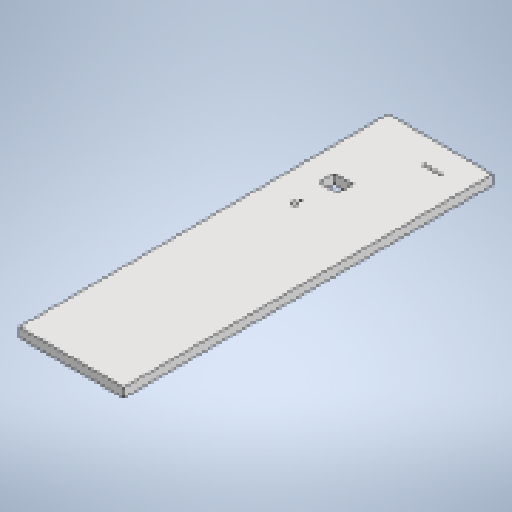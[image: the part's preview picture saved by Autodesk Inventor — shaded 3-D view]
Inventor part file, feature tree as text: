
AUTODESK INVENTOR PART (.ipt)
format: ipt  version: 2025 (Build 290162010, 162A)  size: 158,720 bytes
history: native  units: mm
features: extrude x1, sketch x1
ambient origin geometry x8: Origin, YZ Plane, XZ Plane, XY Plane, X Axis, Y Axis, Z Axis, Center Point
bodies: Solid1 (feature_tree)
feature tree (2):
  extrude  "Extrusion1"  Depth=12000.0mm
  sketch  "Sketch1"  dims[d0=3400.0mm d1=12000.0mm d2=600.0mm d3=500.0mm d4=168.0mm d5=63.0mm d6=1000.0mm d7=800.0mm d8=300.0mm d9=0.0mm d10=2550.0mm d11=3850.0mm d12=200.0mm d13=100.0mm d14=170.0mm d15=170.0mm d16=170.0mm d17=780.0mm d18=780.0mm]
